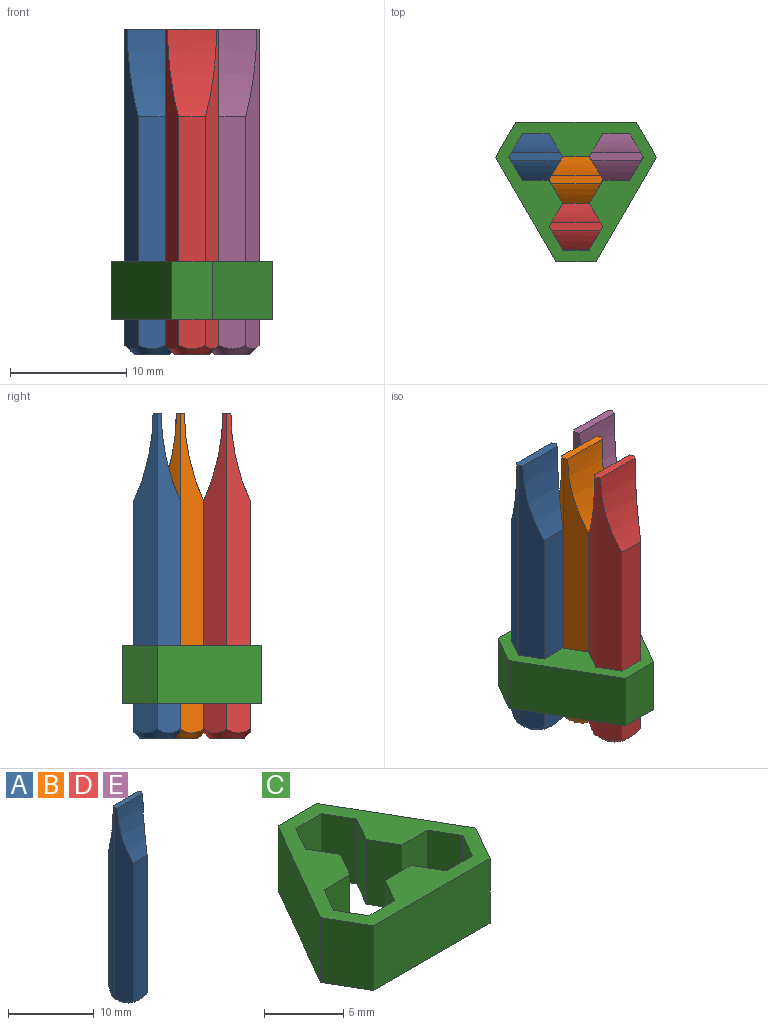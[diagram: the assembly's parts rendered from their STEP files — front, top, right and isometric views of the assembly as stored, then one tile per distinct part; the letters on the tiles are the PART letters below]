
ASSEMBLY  parts=5 mates=6
PART A: 11 faces, bbox 4.6x4.6x28 mm
  f0: plane 20x2.31mm, normal (0,1,0), area 45.9mm2, adj f2,f6,f7,f9
  f1: plane 4.62x0.7mm, normal (0,0,1), area 3.1mm2, adj f2,f3,f5,f6,f7,f8
  f2: plane 27.5x2mm, normal (-0.87,0.5,0), area 53.6mm2, adj f0,f1,f3,f7,f9
  f3: plane 27.5x2mm, normal (-0.87,-0.5,0), area 53.6mm2, adj f1,f2,f4,f8,f9
  f4: plane 20x2.31mm, normal (0,-1,0), area 45.9mm2, adj f3,f5,f8,f9
  f5: plane 27.5x2mm, normal (0.87,-0.5,0), area 53.6mm2, adj f1,f4,f6,f8,f9
  f6: plane 27.5x2mm, normal (0.87,0.5,0), area 53.6mm2, adj f0,f1,f5,f7,f9
  f7: cylinder r=17.87mm len=7.5mm, axis (1,0,0), area 27.7mm2, adj f0,f1,f2,f6
  f8: cylinder r=17.87mm len=7.5mm, axis (1,0,0), area 27.7mm2, adj f1,f3,f4,f5
  f9: cone r=1.5mm half-angle=45deg, axis (0,0,1), area 9.6mm2, adj f0,f2,f3,f4,f5,f6,f10
  f10: plane 3x3mm, normal (0,0,-1), area 7.1mm2, adj f9
PART B: same geometry as A
PART C: 26 faces, bbox 13.9x12x5 mm
  f0: plane 5x2mm, normal (-0.87,-0.5,0), area 11.5mm2, adj f1,f23,f24,f25
  f1: plane 5x2.31mm, normal (0,-1,0), area 11.5mm2, adj f0,f2,f24,f25
  f2: plane 5x2mm, normal (-0.87,-0.5,0), area 11.5mm2, adj f1,f3,f24,f25
  f3: plane 5x2mm, normal (-0.87,0.5,0), area 11.5mm2, adj f2,f4,f24,f25
  f4: plane 5x2.31mm, normal (0,1,0), area 11.5mm2, adj f3,f5,f24,f25
  f5: plane 5x2mm, normal (0.87,0.5,0), area 11.5mm2, adj f4,f6,f24,f25
  f6: plane 5x2.31mm, normal (0,1,0), area 11.5mm2, adj f5,f7,f24,f25
  f7: plane 5x2mm, normal (-0.87,0.5,0), area 11.5mm2, adj f6,f8,f24,f25
  f8: plane 5x2.31mm, normal (0,1,0), area 11.5mm2, adj f7,f9,f24,f25
  f9: plane 5x2mm, normal (0.87,0.5,0), area 11.5mm2, adj f8,f10,f24,f25
  f10: plane 5x2mm, normal (0.87,-0.5,0), area 11.5mm2, adj f9,f11,f24,f25
  f11: plane 5x2.31mm, normal (0,-1,0), area 11.5mm2, adj f10,f12,f24,f25
  f12: plane 5x2mm, normal (0.87,-0.5,0), area 11.5mm2, adj f11,f13,f24,f25
  f13: plane 5x2mm, normal (0.87,0.5,0), area 11.5mm2, adj f12,f14,f24,f25
  f14: plane 5x2mm, normal (0.87,-0.5,0), area 11.5mm2, adj f13,f15,f24,f25
  f15: plane 5x2.31mm, normal (0,-1,0), area 11.5mm2, adj f14,f16,f24,f25
  f16: plane 5x2mm, normal (-0.87,-0.5,0), area 11.5mm2, adj f15,f23,f24,f25
  f17: plane 10.39x5mm, normal (0,-1,0), area 52mm2, adj f18,f22,f24,f25
  f18: plane 5x3mm, normal (0.87,-0.5,0), area 17.3mm2, adj f17,f19,f24,f25
  f19: plane 9x5.2mm, normal (0.87,0.5,0), area 52mm2, adj f18,f20,f24,f25
  f20: plane 5x3.46mm, normal (0,1,0), area 17.3mm2, adj f19,f21,f24,f25
  f21: plane 9x5.2mm, normal (-0.87,0.5,0), area 52mm2, adj f20,f22,f24,f25
  f22: plane 5x3mm, normal (-0.87,-0.5,0), area 17.3mm2, adj f17,f21,f24,f25
  f23: plane 5x2mm, normal (-0.87,0.5,0), area 11.5mm2, adj f0,f16,f24,f25
  f24: plane 13.86x12mm, normal (0,0,1), area 58.9mm2, adj f0,f1,f2,f3,f4,f5,f6,f7
  f25: plane 13.86x12mm, normal (0,0,-1), area 58.9mm2, adj f0,f1,f2,f3,f4,f5,f6,f7
PART D: same geometry as A
PART E: same geometry as A
PLACE A rot(axis=(0,0,1),180deg) t=(-3.46,2,16.46)mm
PLACE B rot(axis=(0,0,-1),180deg) t=(0,0,16.46)mm
PLACE C rot(axis=(1,0,0),180deg) t=(0,0,24.46)mm
PLACE D rot(axis=(0,0,1),180deg) t=(0,-4,16.46)mm
PLACE E rot(axis=(0,0,-1),180deg) t=(3.46,2,16.46)mm
MATE slider B.f9 <-> C.f25  axis (0,0,-1) through (0,0,16.46)mm
MATE slider E.f1 <-> C.f25  axis (0,0,1) through (5.77,2,44.46)mm
MATE planar A.f9 <-> D.f9  axis (0,0,-1) through (-3.46,2,16.46)mm
MATE slider A.f1 <-> C.f25  axis (0,0,1) through (-5.77,2,44.46)mm
MATE slider D.f1 <-> C.f25  axis (0,0,1) through (-2.31,-4,44.46)mm
MATE planar E.f9 <-> D.f9  axis (0,0,-1) through (3.46,2,16.46)mm
